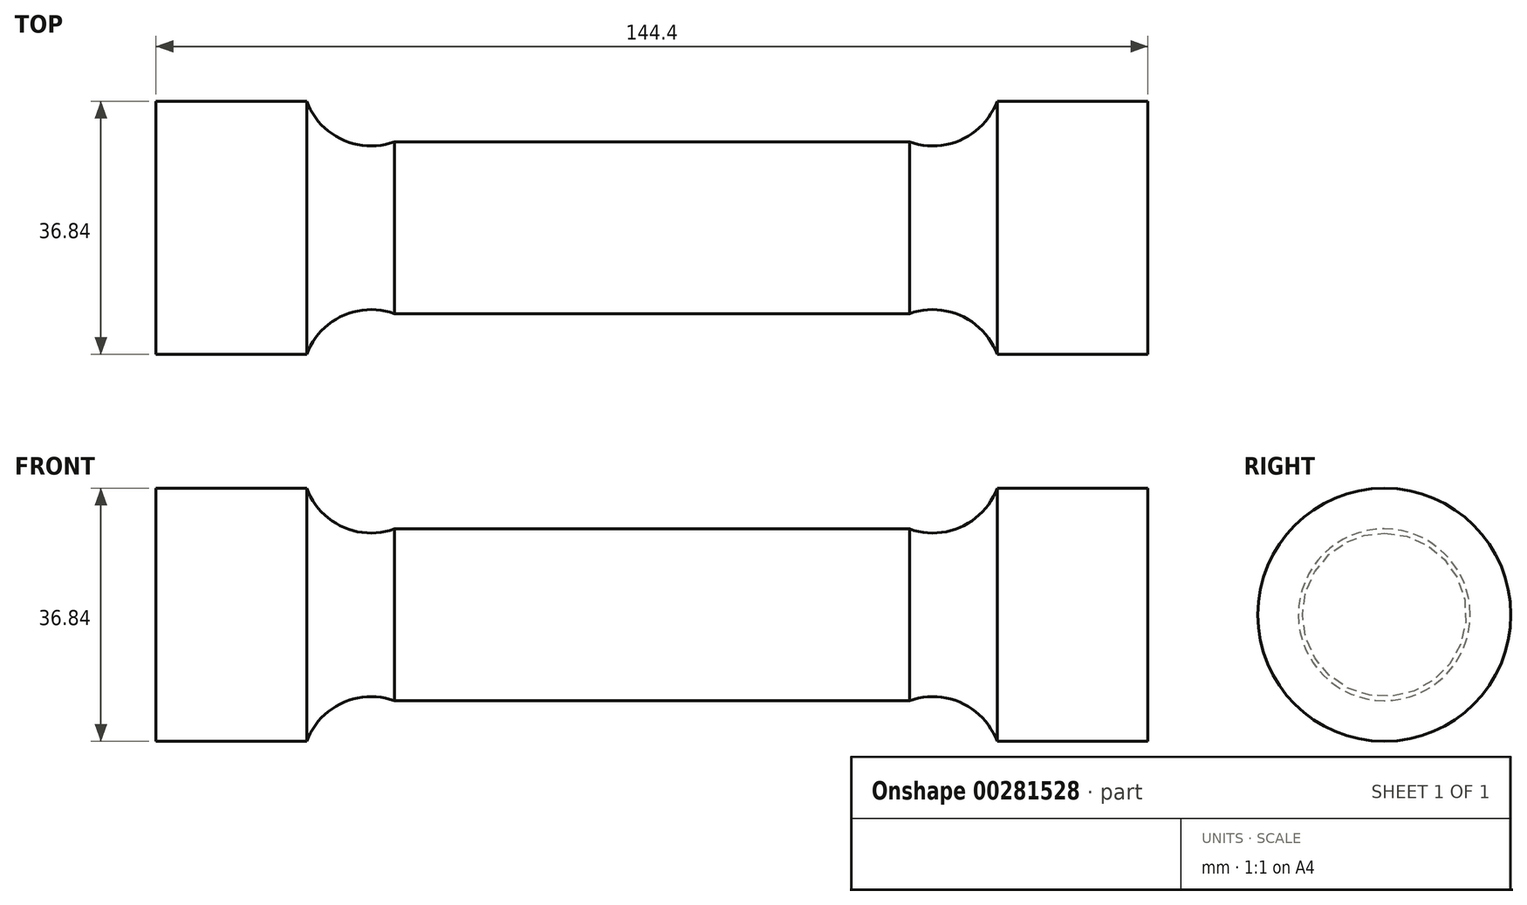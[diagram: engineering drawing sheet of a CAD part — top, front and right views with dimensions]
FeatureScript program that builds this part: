
annotation { "Feature Type Name" : "Feature", "Feature Type Description" : "" }
export const myFeature = defineFeature(function(context is Context, id is Id, definition is map)
    precondition{}
    {
        {
            var Q0;
            Q0=qCreatedBy(makeId("Front.planeOp"),FACE);
            var sketch = newSketch(context, id + "F0", { "sketchPlane" : qUnion([Q0])});
            skLineSegment(sketch, "E0", {"start": v(0, 12.5) * mm, "end": v(37.5, 12.5) * mm});
            skArc(sketch, "E1", {"start": v(37.5, 12.5) * mm, "mid": v(45.1, 12.84) * mm, "end": v(50.26, 18.42) * mm});
            skLineSegment(sketch, "E2", {"start": v(50.26, 18.42) * mm, "end": v(72.2, 18.42) * mm});
            skLineSegment(sketch, "E3", {"start": v(72.2, 18.42) * mm, "end": v(72.2, 0) * mm});
            skLineSegment(sketch, "E4.MirrorCS", {"start": v(0, 12.5) * mm, "end": v(-37.5, 12.5) * mm});
            skLineSegment(sketch, "E5.MirrorCS", {"start": v(-50.26, 18.42) * mm, "end": v(-72.2, 18.42) * mm});
            skLineSegment(sketch, "E6.MirrorCS", {"start": v(-72.2, 18.42) * mm, "end": v(-72.2, 0) * mm});
            skArc(sketch, "E7.MirrorCS", {"start": v(-37.5, 12.5) * mm, "mid": v(-45.1, 12.84) * mm, "end": v(-50.26, 18.42) * mm});
            skLineSegment(sketch, "E8", {"start": v(-72.2, 0) * mm, "end": v(72.2, 0) * mm});
            skSolve(sketch);
        }
        {
            var Q0;
            Q0 = qSketchRegion(id + "F0", true);
            var Q1;
            Q1=sQuery(id+"F0.wireOp",EDGE,"E8");
            revolve(context, id + "F1", {"entities" : qUnion([Q0]), "axis" : qUnion([Q1]), "revolveType" : RevolveType.FULL});
        }
    });
